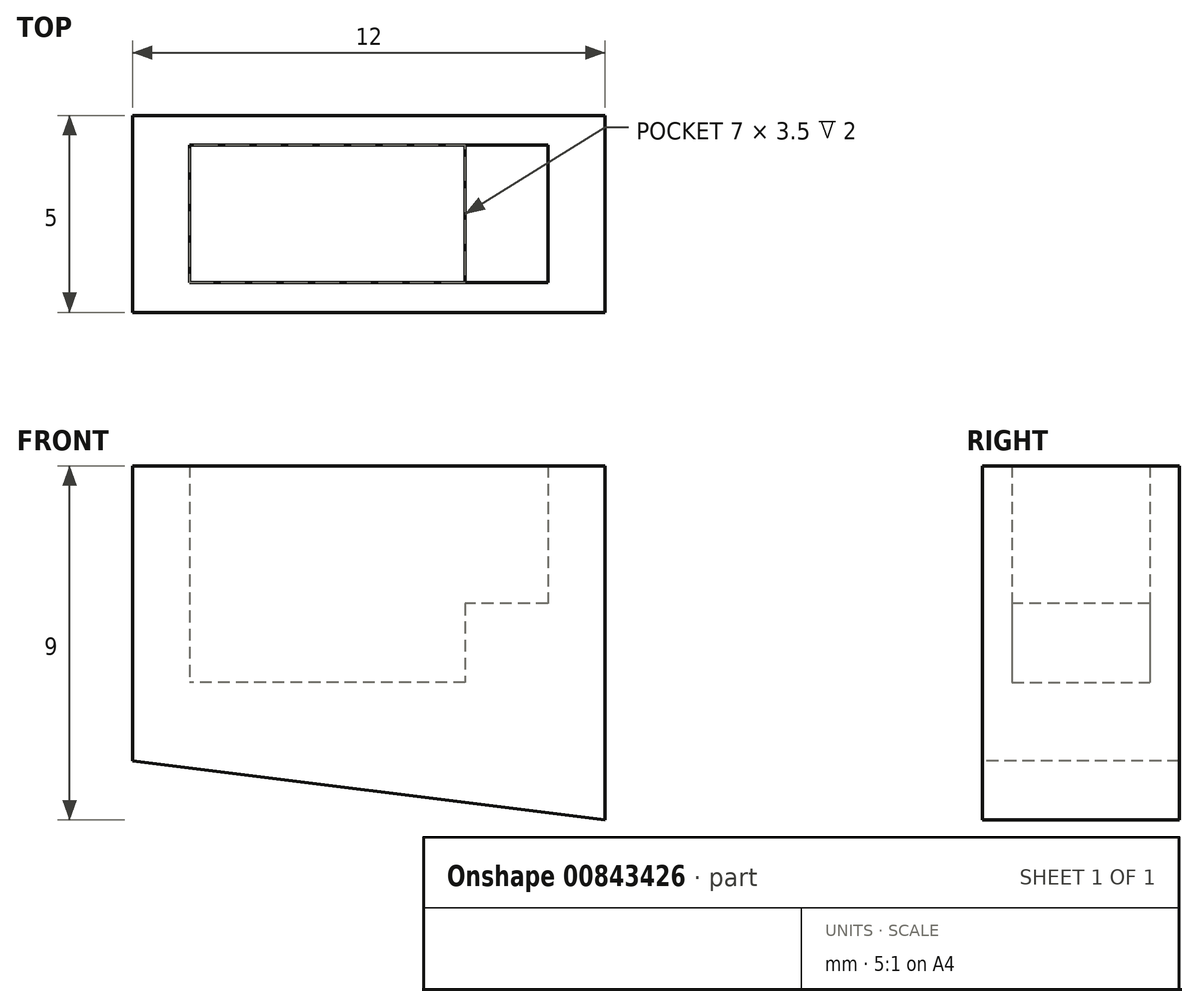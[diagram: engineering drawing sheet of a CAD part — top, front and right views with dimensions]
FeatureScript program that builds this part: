
annotation { "Feature Type Name" : "Feature", "Feature Type Description" : "" }
export const myFeature = defineFeature(function(context is Context, id is Id, definition is map)
    precondition{}
    {
        {
            var Q0;
            Q0=qCreatedBy(makeId("Top.planeOp"),FACE);
            var sketch = newSketch(context, id + "F0", { "sketchPlane" : qUnion([Q0])});
            skLineSegment(sketch, "E0.bottom", {"start": v(6, 2.5) * mm, "end": v(-6, 2.5) * mm});
            skLineSegment(sketch, "E0.top", {"start": v(6, -2.5) * mm, "end": v(-6, -2.5) * mm});
            skLineSegment(sketch, "E0.left", {"start": v(6, 2.5) * mm, "end": v(6, -2.5) * mm});
            skLineSegment(sketch, "E0.right", {"start": v(-6, 2.5) * mm, "end": v(-6, -2.5) * mm});
            skPoint(sketch, "E0.middle", {"position": v(0, 0) * mm});
            skLineSegment(sketch, "E1.bottom", {"start": v(4.55, 1.75) * mm, "end": v(-4.55, 1.75) * mm});
            skLineSegment(sketch, "E1.top", {"start": v(4.55, -1.75) * mm, "end": v(-4.55, -1.75) * mm});
            skLineSegment(sketch, "E1.left", {"start": v(4.55, 1.75) * mm, "end": v(4.55, -1.75) * mm});
            skLineSegment(sketch, "E1.right", {"start": v(-4.55, 1.75) * mm, "end": v(-4.55, -1.75) * mm});
            skLineSegment(sketch, "E2", {"start": v(2.45, -1.75) * mm, "end": v(2.45, 1.75) * mm});
            skSolve(sketch);
        }
        {
            var Q0;
            {var subQ0=sQuery(id+"F0.wireOp",EDGE,"E1.right");Q0=makeQuery(id+"F0.imprint","IMPRINT",FACE,{"disambiguationData":[TD([[makeQuery(id+"F0.imprint","IMPRINT",EDGE,{"derivedFrom":subQ0}),1.0]])]});}
            extrude(context, id + "F1", {"entities" : qUnion([Q0]), "depth" : 2 * mm, "offsetDistance" : 25 * mm});
        }
        {
            var Q0;
            Q0=makeQuery(id+"F0.imprint","IMPRINT",FACE,{"disambiguationData":[TD([[makeQuery(id+"F0.imprint","IMPRINT",EDGE,{"derivedFrom":sQuery(id+"F0.wireOp",EDGE,"E0.bottom")}),1.0]])]});
            extrude(context, id + "F2", {"entities" : qUnion([Q0]), "operationType" : NewBodyOperationType.ADD, "depth" : 7.5 * mm, "offsetDistance" : 25 * mm});
        }
        {
            var Q0;
            Q0=qCreatedBy(makeId("Front.planeOp"),FACE);
            var sketch = newSketch(context, id + "F3", { "sketchPlane" : qUnion([Q0])});
            skLineSegment(sketch, "E3", {"start": v(-6, 0) * mm, "end": v(6, 0) * mm});
            skLineSegment(sketch, "E4", {"start": v(6, 0) * mm, "end": v(6, -1.5) * mm});
            skLineSegment(sketch, "E5", {"start": v(6, -1.5) * mm, "end": v(-6, 0) * mm});
            skSolve(sketch);
        }
        {
            var Q0;
            Q0=makeQuery(id+"F3.imprint","IMPRINT",FACE,{"disambiguationData":[TD([[makeQuery(id+"F3.imprint","IMPRINT",EDGE,{"derivedFrom":sQuery(id+"F3.wireOp",EDGE,"E3")}),-1.0]])]});
            extrude(context, id + "F4", {"entities" : qUnion([Q0]), "operationType" : NewBodyOperationType.ADD, "endBound" : BoundingType.SYMMETRIC, "depth" : 5 * mm, "offsetDistance" : 25 * mm});
        }
        {
            var Q0;
            {var subQ0=sQuery(id+"F0.wireOp",EDGE,"E1.left");Q0=makeQuery(id+"F0.imprint","IMPRINT",FACE,{"disambiguationData":[TD([[makeQuery(id+"F0.imprint","IMPRINT",EDGE,{"derivedFrom":subQ0}),-1.0]])]});}
            extrude(context, id + "F5", {"entities" : qUnion([Q0]), "operationType" : NewBodyOperationType.ADD, "depth" : 4 * mm, "offsetDistance" : 25 * mm});
        }
    });
